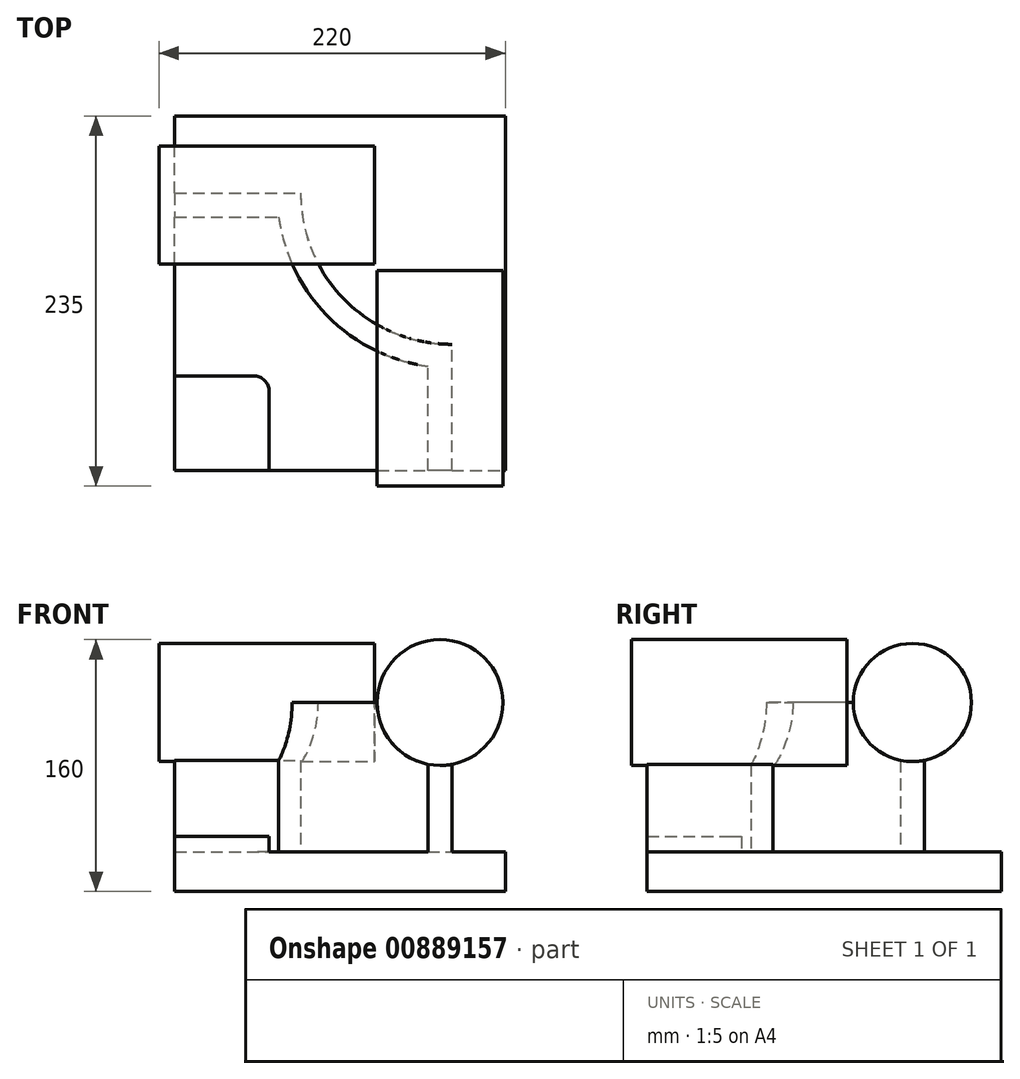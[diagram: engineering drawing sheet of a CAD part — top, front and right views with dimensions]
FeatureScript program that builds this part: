
annotation { "Feature Type Name" : "Feature", "Feature Type Description" : "" }
export const myFeature = defineFeature(function(context is Context, id is Id, definition is map)
    precondition{}
    {
        {
            var Q0;
            Q0=qCreatedBy(makeId("Top.planeOp"),FACE);
            var sketch = newSketch(context, id + "F0", { "sketchPlane" : qUnion([Q0])});
            skLineSegment(sketch, "E0.bottom", {"start": v(-106.69, -44.16) * mm, "end": v(103.31, -44.16) * mm});
            skLineSegment(sketch, "E0.top", {"start": v(-106.69, 180.84) * mm, "end": v(103.31, 180.84) * mm});
            skLineSegment(sketch, "E0.left", {"start": v(-106.69, -44.16) * mm, "end": v(-106.69, 180.84) * mm});
            skLineSegment(sketch, "E0.right", {"start": v(103.31, -44.16) * mm, "end": v(103.31, 180.84) * mm});
            skSolve(sketch);
        }
        {
            var Q0;
            Q0=makeQuery(id+"F0.imprint","IMPRINT",FACE,{"disambiguationData":[TD([[makeQuery(id+"F0.imprint","IMPRINT",EDGE,{"derivedFrom":sQuery(id+"F0.wireOp",EDGE,"E0.bottom")}),1.0]])]});
            extrude(context, id + "F1", {"entities" : qUnion([Q0]), "depth" : 25 * mm, "offsetDistance" : 25 * mm});
        }
        {
            var Q0;
            Q0=makeQuery(id+"F1.opExtrude","CAP_FACE",FACE,{"disambiguationData":[OSD([sQuery(id+"F0.wireOp",EDGE,"E0.bottom"),sQuery(id+"F0.wireOp",EDGE,"E0.top"),sQuery(id+"F0.wireOp",EDGE,"E0.left"),sQuery(id+"F0.wireOp",EDGE,"E0.right")])],"isStart":false});
            var sketch = newSketch(context, id + "F2", { "sketchPlane" : qUnion([Q0])});
            skLineSegment(sketch, "E1", {"start": v(-106.69, 131.84) * mm, "end": v(-26.69, 131.84) * mm});
            skLineSegment(sketch, "E2", {"start": v(0, 180.84) * mm, "end": v(0, -44.16) * mm, "construction": true});
            skLineSegment(sketch, "E3", {"start": v(103.31, 68.34) * mm, "end": v(-106.69, 68.34) * mm, "construction": true});
            skLineSegment(sketch, "E4", {"start": v(-106.69, 68.34) * mm, "end": v(-77.18, 68.34) * mm});
            skLineSegment(sketch, "E5", {"start": v(69.31, -44.16) * mm, "end": v(69.31, 35.84) * mm});
            skArc(sketch, "E6", {"start": v(-26.69, 131.84) * mm, "mid": v(1.43, 63.96) * mm, "end": v(69.31, 35.84) * mm});
            skLineSegment(sketch, "E7", {"start": v(69.31, 35.84) * mm, "end": v(69.31, 131.84) * mm, "construction": true});
            skLineSegment(sketch, "E8", {"start": v(-26.69, 131.84) * mm, "end": v(69.31, 131.84) * mm, "construction": true});
            skLineSegment(sketch, "E9.0", {"start": v(-106.69, 116.84) * mm, "end": v(-40.67, 116.84) * mm});
            skArc(sketch, "E9.1", {"start": v(-40.67, 116.84) * mm, "mid": v(-9.17, 53.35) * mm, "end": v(54.31, 21.86) * mm});
            skLineSegment(sketch, "E9.2", {"start": v(54.31, -44.16) * mm, "end": v(54.31, 21.86) * mm});
            skLineSegment(sketch, "E10.0", {"start": v(-106.69, -44.16) * mm, "end": v(-106.69, 180.84) * mm});
            skLineSegment(sketch, "E11.0", {"start": v(-106.69, -44.16) * mm, "end": v(103.31, -44.16) * mm});
            skSolve(sketch);
        }
        {
            var Q0;
            {var subQ2=sQuery(id+"F2.wireOp",EDGE,"E1");Q0=makeQuery(id+"F2.imprint","IMPRINT",FACE,{"disambiguationData":[TD([[makeQuery(id+"F2.imprint","IMPRINT",EDGE,{"derivedFrom":subQ2}),-1.0]])]});}
            extrude(context, id + "F3", {"entities" : qUnion([Q0]), "operationType" : NewBodyOperationType.ADD, "depth" : 95 * mm, "offsetDistance" : 25 * mm});
        }
        {
            var Q0;
            Q0=makeQuery(id+"F3.boolean.opBoolean","MERGE",FACE,{"derivedFrom":[makeQuery(id+"F1.opExtrude","SWEPT_FACE",FACE,{"disambiguationData":[OSD([sQuery(id+"F0.wireOp",EDGE,"E0.left")])]}),makeQuery(id+"F3.opExtrude","SWEPT_FACE",FACE,{"disambiguationData":[OSD([sQuery(id+"F2.wireOp",EDGE,"E10.0")])]})]});
            var sketch = newSketch(context, id + "F4", { "sketchPlane" : qUnion([Q0])});
            skCircle(sketch, "E12", {"center": v(-124.34, 120) * mm, "radius": 37.5 * mm});
            skSolve(sketch);
        }
        {
            var Q0;
            Q0 = qSketchRegion(id + "F4", true);
            extrude(context, id + "F5", {"entities" : qUnion([Q0]), "operationType" : NewBodyOperationType.ADD, "depth" : 10 * mm, "offsetDistance" : 25 * mm, "hasSecondDirection" : true, "secondDirectionOppositeDirection" : true, "secondDirectionDepth" : (137 - 10) * mm});
        }
        {
            var Q0;
            Q0=makeQuery(id+"F3.boolean.opBoolean","MERGE",FACE,{"derivedFrom":[makeQuery(id+"F1.opExtrude","SWEPT_FACE",FACE,{"disambiguationData":[OSD([sQuery(id+"F0.wireOp",EDGE,"E0.bottom")])]}),makeQuery(id+"F3.opExtrude","SWEPT_FACE",FACE,{"disambiguationData":[OSD([sQuery(id+"F2.wireOp",EDGE,"E11.0")])]})]});
            var sketch = newSketch(context, id + "F6", { "sketchPlane" : qUnion([Q0])});
            skCircle(sketch, "E13", {"center": v(61.81, 120) * mm, "radius": 40 * mm});
            skSolve(sketch);
        }
        {
            var Q0;
            Q0 = qSketchRegion(id + "F6", true);
            extrude(context, id + "F7", {"entities" : qUnion([Q0]), "operationType" : NewBodyOperationType.ADD, "depth" : 10 * mm, "offsetDistance" : 25 * mm, "hasSecondDirection" : true, "secondDirectionOppositeDirection" : true, "secondDirectionDepth" : (137 - 10) * mm});
        }
        {
            var Q0;
            {var subQ0=sQuery(id+"F0.wireOp",EDGE,"E0.left");var subQ1=sQuery(id+"F0.wireOp",EDGE,"E0.bottom");Q0=makeQuery(id+"F3.boolean.opBoolean","SPLIT",FACE,{"disambiguationData":[TD([makeQuery(id+"F3.opExtrude","SWEPT_FACE",FACE,{"disambiguationData":[OSD([sQuery(id+"F2.wireOp",EDGE,"E9.0")])]})])],"derivedFrom":makeQuery(id+"F1.opExtrude","CAP_FACE",FACE,{"disambiguationData":[OSD([subQ1,sQuery(id+"F0.wireOp",EDGE,"E0.top"),subQ0,sQuery(id+"F0.wireOp",EDGE,"E0.right")])],"isStart":false})});}
            var sketch = newSketch(context, id + "F8", { "sketchPlane" : qUnion([Q0])});
            skLineSegment(sketch, "E14.bottom", {"start": v(-106.69, -44.16) * mm, "end": v(-46.69, -44.16) * mm});
            skLineSegment(sketch, "E14.top", {"start": v(-106.69, 15.84) * mm, "end": v(-46.69, 15.84) * mm});
            skLineSegment(sketch, "E14.left", {"start": v(-106.69, -44.16) * mm, "end": v(-106.69, 15.84) * mm});
            skLineSegment(sketch, "E14.right", {"start": v(-46.69, -44.16) * mm, "end": v(-46.69, 15.84) * mm});
            skSolve(sketch);
        }
        {
            var Q0;
            Q0=makeQuery(id+"F8.imprint","IMPRINT",FACE,{"disambiguationData":[TD([[makeQuery(id+"F8.imprint","IMPRINT",EDGE,{"derivedFrom":sQuery(id+"F8.wireOp",EDGE,"E14.bottom")}),1.0]])]});
            extrude(context, id + "F9", {"entities" : qUnion([Q0]), "operationType" : NewBodyOperationType.ADD, "depth" : 10 * mm, "offsetDistance" : 25 * mm});
        }
        {
            var Q0;
            Q0=makeQuery(id+"F9.opExtrude","SWEPT_EDGE",EDGE,{"disambiguationData":[OSD([sQuery(id+"F8.wireOp",EDGE,"E14.top"),sQuery(id+"F8.wireOp",EDGE,"E14.right")])]});
            fillet(context, id + "F10", {"entities" : qUnion([Q0]), "radius" : 10 * mm, "tangentPropagation" : true, "allowEdgeOverflow" : false});
        }
    });
